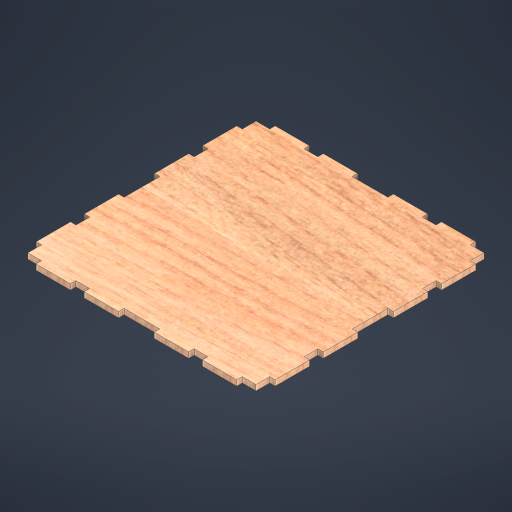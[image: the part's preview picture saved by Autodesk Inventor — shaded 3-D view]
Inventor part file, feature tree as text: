
AUTODESK INVENTOR PART (.ipt)
format: ipt  version: 2024.1 (Build 281209000, 209)  size: 463,360 bytes
history: native  units: mm
features: extrude x1, sketch x1
ambient origin geometry x8: Origin, YZ Plane, XZ Plane, XY Plane, X Axis, Y Axis, Z Axis, Center Point
bodies: Solid1 (feature_tree)
feature tree (2):
  extrude  "Extrusion1"  Depth=100.0mm
  sketch  "Sketch1"  dims[d0=12.0mm d1=100.0mm d3=16.0mm d4=100.0mm d6=16.0mm d9=5.0mm d10=5.0mm d11=4.0mm d12=4.0mm d13=10.0mm d14=10.0mm d15=25.0mm d16=4.0mm d17=25.0mm d18=10.0mm d19=25.0mm d20=10.0mm d21=25.0mm d22=4.0mm d23=40.0mm d25=360.0deg d27=4.0mm d28=0.0mm]
